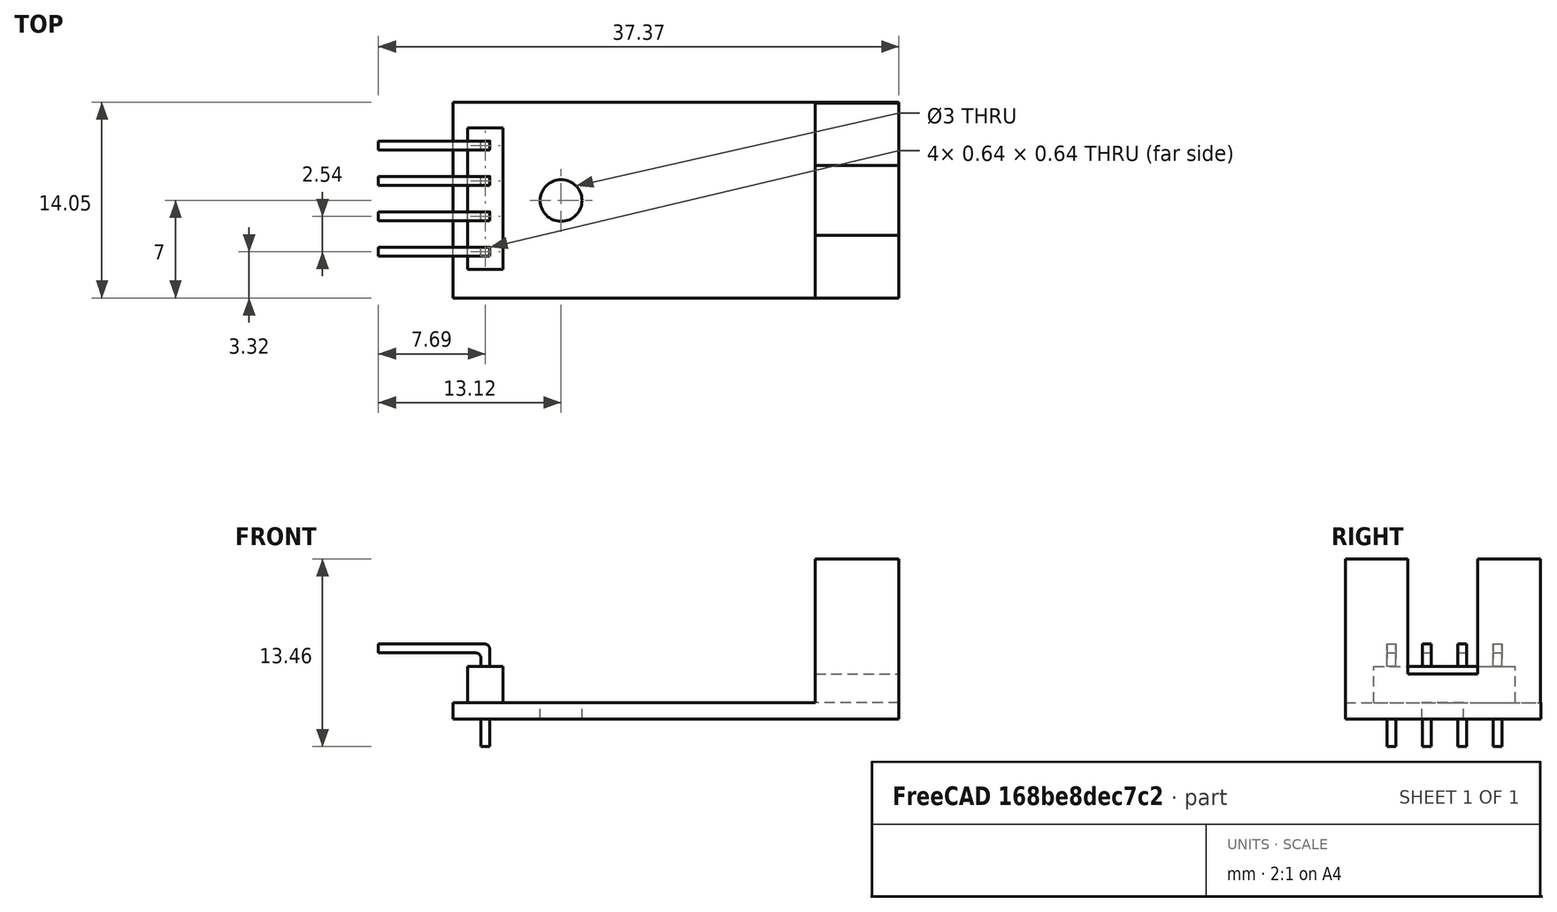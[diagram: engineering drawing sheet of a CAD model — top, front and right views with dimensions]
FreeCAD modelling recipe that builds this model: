
FCSTD DOCUMENT  (FreeCAD 0.14R2935 (Git))
Label: j34-optocoupler-lm393
License: CC-BY 3.0
LicenseURL: http://creativecommons.org/licenses/by/3.0/
objects: Part::Box×15, Part::Fuse×12, PartDesign::Fillet×8, Part::Cut×3, Part::Cylinder×1
note: 39 computed .brp shape members not serialized (recipe doc carries the construction recipe); baked Part::Feature solids carry a one-line shape summary decoded from their .brp

FEATURE [Part::Box] Box
  Height = 1.2
  Length = 32
  Width = 14.05
FEATURE [Part::Box] Box001
  Height = 11.5
  Length = 6
  Placement = pos=(26,9.5,0) rot=(0,0,1;0rad)
  Width = 4.5
FEATURE [Part::Box] Box002
  Height = 11.5
  Length = 6
  Placement = pos=(26,0,0) rot=(0,0,1;0rad)
  Width = 4.5
FEATURE [Part::Box] Box003
  Height = 3.25
  Length = 6
  Placement = pos=(26,4.5,0) rot=(0,0,1;0rad)
  Width = 5
FEATURE [Part::Fuse] Fusion
  Base = -> Box
  Tool = -> Box001
FEATURE [Part::Fuse] Fusion001
  Base = -> Fusion
  Tool = -> Box002
FEATURE [Part::Fuse] Fusion002
  Base = -> Fusion001
  Tool = -> Box003
FEATURE [Part::Box] Box004
  Height = 9.9
  Length = 0.64
  Width = 0.64
FEATURE [Part::Box] Box005
  Height = 9.9
  Length = 0.64
  Placement = pos=(-9.9,0,9.9) rot=(0,1,0;1.5708rad)
  Width = 0.64
FEATURE [Part::Box] Box006
  Height = 9.9
  Length = 0.64
  Placement = pos=(0,2.54,0) rot=(0,0,1;0rad)
  Width = 0.64
FEATURE [Part::Box] Box007
  Height = 9.9
  Length = 0.64
  Placement = pos=(-9.9,2.54,9.9) rot=(0,1,0;1.5708rad)
  Width = 0.64
FEATURE [Part::Box] Box008
  Height = 9.9
  Length = 0.64
  Placement = pos=(0,5.08,0) rot=(0,0,1;0rad)
  Width = 0.64
FEATURE [Part::Box] Box009
  Height = 9.9
  Length = 0.64
  Placement = pos=(-9.9,5.08,9.9) rot=(0,1,0;1.5708rad)
  Width = 0.64
FEATURE [Part::Box] Box010
  Height = 9.9
  Length = 0.64
  Placement = pos=(0,7.62,0) rot=(0,0,1;0rad)
  Width = 0.64
FEATURE [Part::Box] Box011
  Height = 9.9
  Length = 0.64
  Placement = pos=(-9.9,7.62,9.9) rot=(0,1,0;1.5708rad)
  Width = 0.64
FEATURE [Part::Fuse] Fusion003
  Base = -> Box004
  Tool = -> Box005
FEATURE [Part::Fuse] Fusion004
  Base = -> Fusion003
  Tool = -> Box006
FEATURE [Part::Fuse] Fusion005
  Base = -> Fusion004
  Tool = -> Box007
FEATURE [Part::Fuse] Fusion006
  Base = -> Fusion005
  Tool = -> Box008
FEATURE [Part::Fuse] Fusion007
  Base = -> Fusion006
  Tool = -> Box009
FEATURE [Part::Fuse] Fusion008
  Base = -> Fusion007
  Tool = -> Box010
FEATURE [Part::Fuse] Fusion009
  Base = -> Fusion008
  Tool = -> Box011
FEATURE [Part::Box] Box012
  Height = 2.6
  Length = 2.54
  Placement = pos=(-0.95,-0.95,5.69) rot=(0,0,1;0rad)
  Width = 10.16
FEATURE [Part::Fuse] Fusion010
  Base = -> Fusion009
  Tool = -> Box012
FEATURE [PartDesign::Fillet] Fillet
  Base = -> Fusion010 [Edge81]
  Radius = 0.4
FEATURE [PartDesign::Fillet] Fillet001
  Base = -> Fillet [Edge72]
  Radius = 0.4
FEATURE [PartDesign::Fillet] Fillet002
  Base = -> Fillet001 [Edge62]
  Radius = 0.4
FEATURE [PartDesign::Fillet] Fillet003
  Base = -> Fillet002 [Edge52]
  Radius = 0.4
FEATURE [PartDesign::Fillet] Fillet004
  Base = -> Fillet003 [Edge32]
  Radius = 0.4
FEATURE [PartDesign::Fillet] Fillet005
  Base = -> Fillet004 [Edge57]
  Radius = 0.4
FEATURE [PartDesign::Fillet] Fillet006
  Base = -> Fillet005 [Edge70]
  Radius = 0.4
FEATURE [PartDesign::Fillet] Fillet007
  Base = -> Fillet006 [Edge84]
  Radius = 0.4
FEATURE [Part::Box] Box013
  Height = 2.53
  Length = 2.53
  Placement = pos=(-9.9,-1,8.9) rot=(0,0,1;0rad)
  Width = 10
FEATURE [Part::Cut] Cut
  Base = -> Fillet007
  Tool = -> Box013
FEATURE [Part::Box] Box014
  Height = 2.54
  Length = 2.54
  Placement = pos=(-0.5,-1,0) rot=(0,0,1;0rad)
  Width = 10
FEATURE [Part::Cut] Cut001
  Base = -> Cut
  Placement = pos=(2,3,-4.5) rot=(0,0,1;0rad)
  Tool = -> Box014
FEATURE [Part::Fuse] Fusion011
  Base = -> Fusion002
  Tool = -> Cut001
FEATURE [Part::Cylinder] Cylinder
  Angle = 360
  Height = 10
  Placement = pos=(7.75,7,0) rot=(0,0,1;0rad)
  Radius = 1.5
FEATURE [Part::Cut] Cut002
  Base = -> Fusion011
  Tool = -> Cylinder
